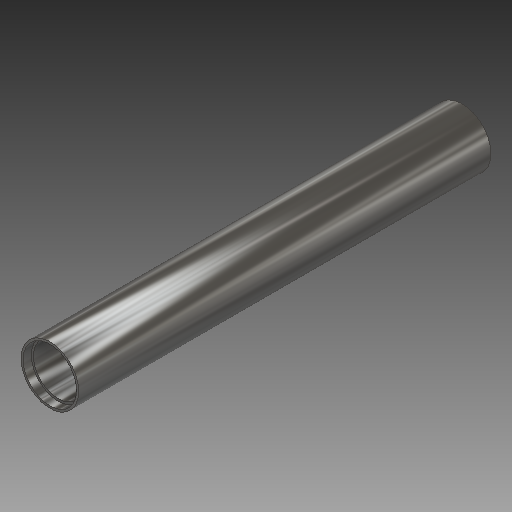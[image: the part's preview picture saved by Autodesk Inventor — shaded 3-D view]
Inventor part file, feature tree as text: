
AUTODESK INVENTOR PART (.ipt)
format: ipt  version: 2019 (Build 230136000, 136)  size: 141,824 bytes
history: native  units: in
note: dims shown in document units (in); Inventor stores cm internally (conversion verified against a paired STEP export)
features: other x3, sketch x3
ambient origin geometry x8: Origin, YZ Plane, XZ Plane, XY Plane, X Axis, Y Axis, Z Axis, Center Point
bodies: Solid1 (feature_tree)
feature tree (6):
  other  "project rolller 1 part2.ipt"
  other  "Solid1::project rolller 1 part2.ipt"
  other  "TaggingFeature1"
  sketch  "Sketch1"  dims[d0=0.3937in]
  sketch  "Sketch2"
  sketch  "Sketch3"
